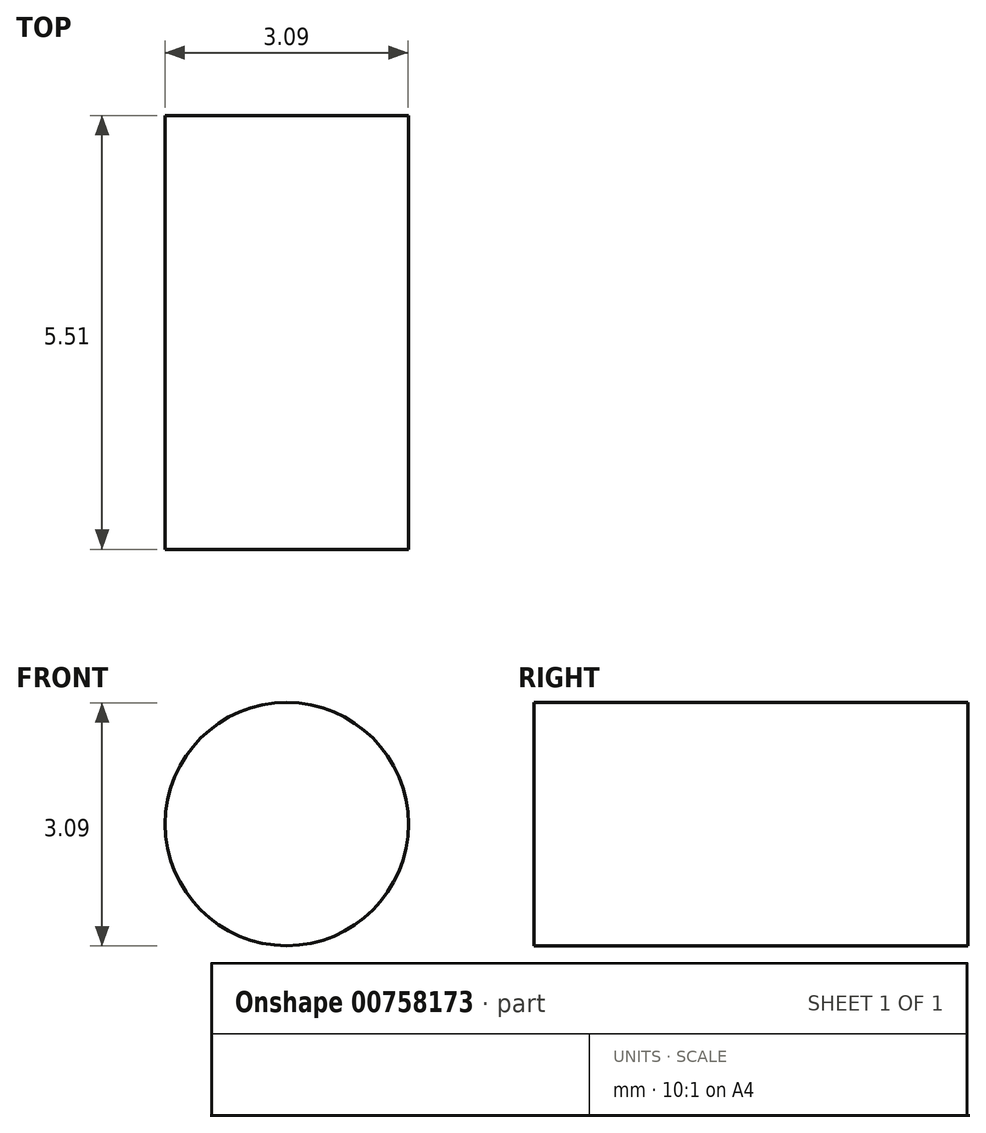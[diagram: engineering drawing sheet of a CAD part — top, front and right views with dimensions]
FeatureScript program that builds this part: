
annotation { "Feature Type Name" : "Feature", "Feature Type Description" : "" }
export const myFeature = defineFeature(function(context is Context, id is Id, definition is map)
    precondition{}
    {
        {
            var Q0;
            Q0=qCreatedBy(makeId("Front.planeOp"),FACE);
            var sketch = newSketch(context, id + "F0", { "sketchPlane" : qUnion([Q0])});
            skCircle(sketch, "E0", {"center": v(-27.05, 22.44) * mm, "radius": 1.55 * mm});
            skSolve(sketch);
        }
        {
            var Q0;
            Q0=makeQuery(id+"F0.imprint","IMPRINT",FACE,{"disambiguationData":[TD([[makeQuery(id+"F0.imprint","IMPRINT",EDGE,{"derivedFrom":sQuery(id+"F0.wireOp",EDGE,"E0")}),1.0]])]});
            extrude(context, id + "F1", {"entities" : qUnion([Q0]), "depth" : 5.5 * mm, "offsetDistance" : 25.4 * mm});
        }
    });
